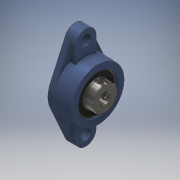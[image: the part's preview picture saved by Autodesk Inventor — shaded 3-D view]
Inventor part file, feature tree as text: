
AUTODESK INVENTOR PART (.ipt)
format: ipt  version: 2017 (Build 210142000, 142)  size: 782,336 bytes
history: native  units: mm
features: other x16, sketch x1
ambient origin geometry x8: Origin, YZ Plane, XZ Plane, XY Plane, X Axis, Y Axis, Z Axis, Center Point
bodies: Body1 (feature_tree)
feature tree (17):
  other  "UCFL201-08 TWO-BOLT FLANGE BEARING.iam"
  other  "inafag_ucfl201-08_8iwm4vnff3g45oi9d3mfhiexc_1.ipt:1"
  other  "inafag_ucfl201-08_8iwm4vnff3g45oi9d3mfhiexc_2.ipt:1"
  other  "inafag_ucfl201-08_8iwm4vnff3g45oi9d3mfhiexc_3.ipt:1"
  other  "inafag_ucfl201-08_8iwm4vnff3g45oi9d3mfhiexc_4.ipt:1"
  other  "inafag_ucfl201-08_8iwm4vnff3g45oi9d3mfhiexc_5.ipt:1"
  other  "inafag_ucfl201-08_8iwm4vnff3g45oi9d3mfhiexc_6.ipt:1"
  other  "inafag_ucfl201-08_8iwm4vnff3g45oi9d3mfhiexc_7.ipt:1"
  other  "inafag_ucfl201-08_8iwm4vnff3g45oi9d3mfhiexc_8.ipt:1"
  other  "inafag_ucfl201-08_8iwm4vnff3g45oi9d3mfhiexc_9.ipt:1"
  other  "inafag_ucfl201-08_8iwm4vnff3g45oi9d3mfhiexc_10.ipt:1"
  other  "inafag_ucfl201-08_8iwm4vnff3g45oi9d3mfhiexc_11.ipt:1"
  other  "inafag_ucfl201-08_8iwm4vnff3g45oi9d3mfhiexc_12.ipt:1"
  other  "inafag_ucfl201-08_8iwm4vnff3g45oi9d3mfhiexc_13.ipt:1"
  other  "inafag_ucfl201-08_8iwm4vnff3g45oi9d3mfhiexc_14.ipt:1"
  other  "Sólido1"
  sketch  "Boceto1"  dims[d0=10.0mm]
